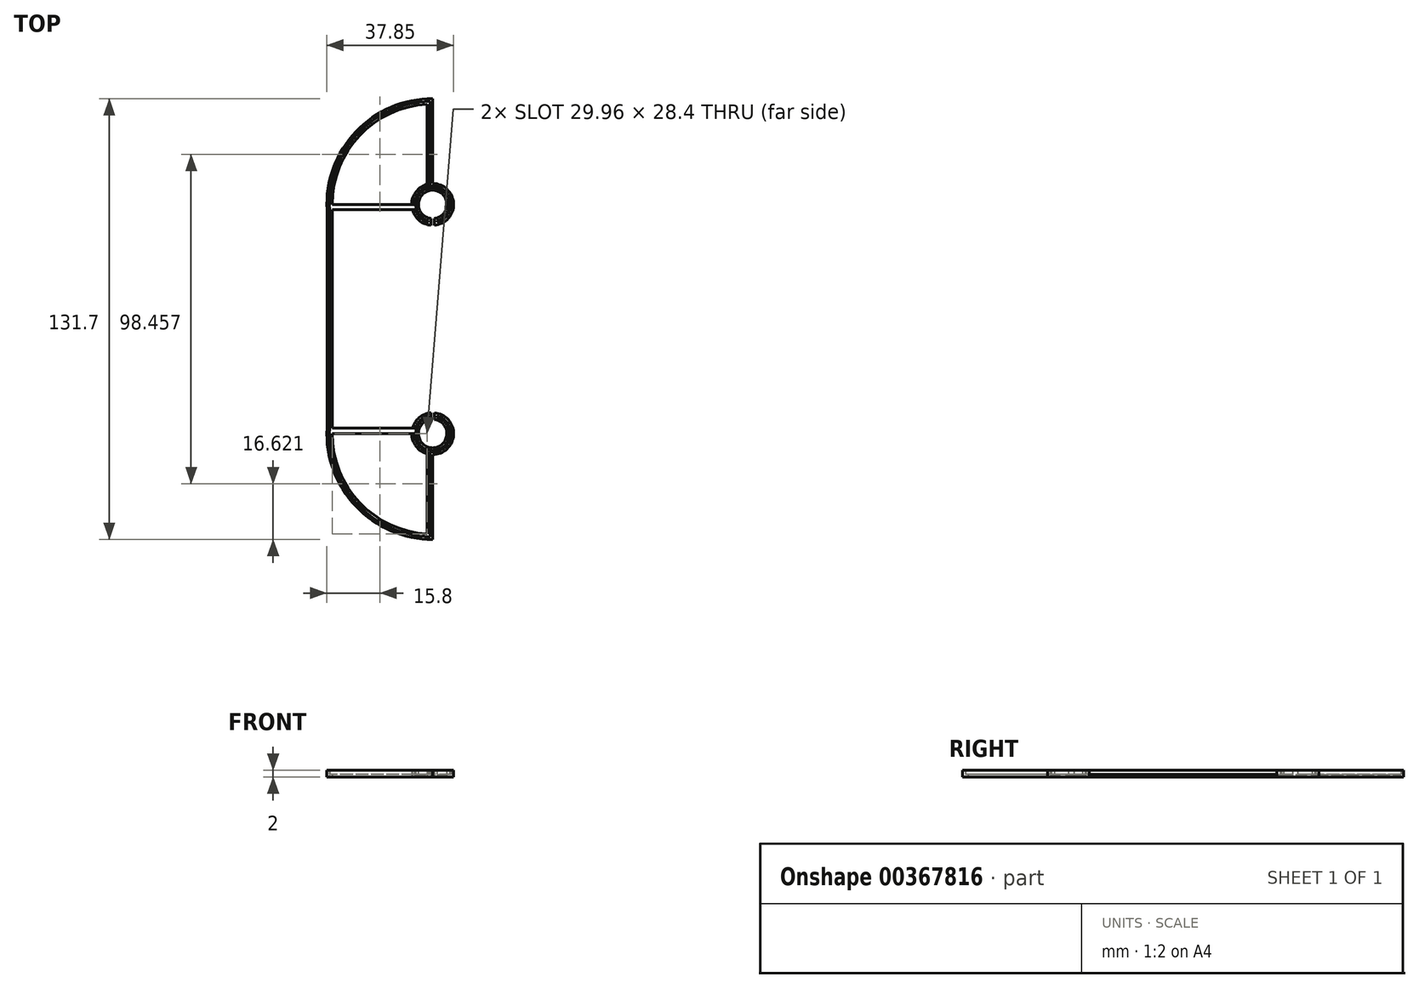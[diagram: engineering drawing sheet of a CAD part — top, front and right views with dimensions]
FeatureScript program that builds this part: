
annotation { "Feature Type Name" : "Feature", "Feature Type Description" : "" }
export const myFeature = defineFeature(function(context is Context, id is Id, definition is map)
    precondition{}
    {
        {
            var Q0;
            Q0=qCreatedBy(makeId("Top.planeOp"),FACE);
            var sketch = newSketch(context, id + "F0", { "sketchPlane" : qUnion([Q0])});
            skLineSegment(sketch, "E0.bottom", {"start": v(-34.25, -34.25) * mm, "end": v(34.25, -34.25) * mm, "construction": true});
            skLineSegment(sketch, "E0.top", {"start": v(-34.25, 34.25) * mm, "end": v(34.25, 34.25) * mm, "construction": true});
            skLineSegment(sketch, "E0.left", {"start": v(-34.25, -34.25) * mm, "end": v(-34.25, 34.25) * mm, "construction": true});
            skLineSegment(sketch, "E0.right", {"start": v(34.25, -34.25) * mm, "end": v(34.25, 34.25) * mm, "construction": true});
            skPoint(sketch, "E0.middle", {"position": v(0, 0) * mm});
            skLineSegment(sketch, "E1", {"start": v(0, 0) * mm, "end": v(0, 34.25) * mm, "construction": true});
            skLineSegment(sketch, "E2", {"start": v(0, 0) * mm, "end": v(-34.25, 0) * mm, "construction": true});
            skCircle(sketch, "E3", {"center": v(-34.25, 34.25) * mm, "radius": 4.25 * mm});
            skCircle(sketch, "E4", {"center": v(-34.25, 34.25) * mm, "radius": 6.25 * mm});
            skLineSegment(sketch, "E5", {"start": v(-34.75, 30.03) * mm, "end": v(-34.75, 28.02) * mm});
            skLineSegment(sketch, "E6.MirrorCS", {"start": v(-33.75, 30.03) * mm, "end": v(-33.75, 28.02) * mm});
            skCircle(sketch, "E7", {"center": v(-34.25, 34.25) * mm, "radius": 30 * mm, "construction": true});
            skCircle(sketch, "E8.MirrorC", {"center": v(34.25, 34.25) * mm, "radius": 6.25 * mm});
            skCircle(sketch, "E9.MirrorC", {"center": v(34.25, 34.25) * mm, "radius": 4.25 * mm});
            skCircle(sketch, "E10.MirrorC", {"center": v(34.25, 34.25) * mm, "radius": 30 * mm, "construction": true});
            skCircle(sketch, "E11.MirrorC", {"center": v(-34.25, -34.25) * mm, "radius": 4.25 * mm});
            skCircle(sketch, "E12.MirrorC", {"center": v(-34.25, -34.25) * mm, "radius": 6.25 * mm});
            skCircle(sketch, "E13.MirrorC", {"center": v(-34.25, -34.25) * mm, "radius": 30 * mm, "construction": true});
            skCircle(sketch, "E14.MirrorC", {"center": v(34.25, -34.25) * mm, "radius": 30 * mm, "construction": true});
            skCircle(sketch, "E15.MirrorC", {"center": v(34.25, -34.25) * mm, "radius": 6.25 * mm});
            skCircle(sketch, "E16.MirrorC", {"center": v(34.25, -34.25) * mm, "radius": 4.25 * mm});
            skLineSegment(sketch, "E17.MirrorCS", {"start": v(33.75, 30.03) * mm, "end": v(33.75, 28.02) * mm});
            skLineSegment(sketch, "E18.MirrorCS", {"start": v(34.75, 30.03) * mm, "end": v(34.75, 28.02) * mm});
            skLineSegment(sketch, "E19.MirrorCS", {"start": v(-34.75, -30.03) * mm, "end": v(-34.75, -28.02) * mm});
            skLineSegment(sketch, "E20.MirrorCS", {"start": v(-33.75, -30.03) * mm, "end": v(-33.75, -28.02) * mm});
            skLineSegment(sketch, "E21.MirrorCS", {"start": v(33.75, -30.03) * mm, "end": v(33.75, -28.02) * mm});
            skLineSegment(sketch, "E22.MirrorCS", {"start": v(34.75, -30.03) * mm, "end": v(34.75, -28.02) * mm});
            skLineSegment(sketch, "E23", {"start": v(-34.25, 40.5) * mm, "end": v(-34.25, 64.25) * mm});
            skLineSegment(sketch, "E24", {"start": v(-35.85, 40.3) * mm, "end": v(-35.85, 64.2) * mm});
            skLineSegment(sketch, "E25", {"start": v(-40.5, 34.25) * mm, "end": v(-64.25, 34.25) * mm});
            skLineSegment(sketch, "E26", {"start": v(-40.3, 32.65) * mm, "end": v(-64.2, 32.65) * mm});
            skArc(sketch, "E27", {"start": v(-34.25, 64.25) * mm, "mid": v(-56.02, 54.89) * mm, "end": v(-64.2, 32.65) * mm});
            skLineSegment(sketch, "E28", {"start": v(-34.25, 64.25) * mm, "end": v(-34.25, 65.85) * mm});
            skLineSegment(sketch, "E29", {"start": v(-64.2, 32.65) * mm, "end": v(-65.8, 32.65) * mm});
            skArc(sketch, "E30", {"start": v(-34.25, 65.85) * mm, "mid": v(-57.15, 56.02) * mm, "end": v(-65.8, 32.65) * mm});
            skLineSegment(sketch, "E31.MirrorCS", {"start": v(-40.3, -32.65) * mm, "end": v(-64.2, -32.65) * mm});
            skLineSegment(sketch, "E32.MirrorCS", {"start": v(-40.5, -34.25) * mm, "end": v(-64.25, -34.25) * mm});
            skLineSegment(sketch, "E33.MirrorCS", {"start": v(-64.2, -32.65) * mm, "end": v(-65.8, -32.65) * mm});
            skArc(sketch, "E34.MirrorCS", {"start": v(-34.25, -65.85) * mm, "mid": v(-57.15, -56.02) * mm, "end": v(-65.8, -32.65) * mm});
            skArc(sketch, "E35.MirrorCS", {"start": v(-34.25, -64.25) * mm, "mid": v(-56.02, -54.89) * mm, "end": v(-64.2, -32.65) * mm});
            skLineSegment(sketch, "E36.MirrorCS", {"start": v(-35.85, -40.3) * mm, "end": v(-35.85, -64.2) * mm});
            skLineSegment(sketch, "E37.MirrorCS", {"start": v(-34.25, -40.5) * mm, "end": v(-34.25, -64.25) * mm});
            skLineSegment(sketch, "E38.MirrorCS", {"start": v(-34.25, -64.25) * mm, "end": v(-34.25, -65.85) * mm});
            skLineSegment(sketch, "E39", {"start": v(-65.8, 32.65) * mm, "end": v(-65.8, -32.65) * mm});
            skLineSegment(sketch, "E40", {"start": v(-64.2, -32.65) * mm, "end": v(-64.2, 32.65) * mm});
            skSolve(sketch);
        }
        {
            var Q0;
            {var subQ0=sQuery(id+"F0.wireOp",EDGE,"E31.MirrorCS");Q0=makeQuery(id+"F0.imprint","IMPRINT",FACE,{"disambiguationData":[TD([[makeQuery(id+"F0.imprint","IMPRINT",EDGE,{"derivedFrom":subQ0}),1.0]])]});}
            var Q1;
            {var subQ5=sQuery(id+"F0.wireOp",EDGE,"E19.MirrorCS");Q1=makeQuery(id+"F0.imprint","IMPRINT",FACE,{"disambiguationData":[TD([[makeQuery(id+"F0.imprint","IMPRINT",EDGE,{"derivedFrom":subQ5}),1.0]])]});}
            var Q2;
            {var subQ0=sQuery(id+"F0.wireOp",EDGE,"E36.MirrorCS");Q2=makeQuery(id+"F0.imprint","IMPRINT",FACE,{"disambiguationData":[TD([[makeQuery(id+"F0.imprint","IMPRINT",EDGE,{"derivedFrom":subQ0}),1.0]])]});}
            var Q3;
            {var subQ4=sQuery(id+"F0.wireOp",EDGE,"E33.MirrorCS");Q3=makeQuery(id+"F0.imprint","IMPRINT",FACE,{"disambiguationData":[TD([[makeQuery(id+"F0.imprint","IMPRINT",EDGE,{"derivedFrom":subQ4}),1.0]])]});}
            var Q4;
            Q4=makeQuery(id+"F0.imprint","IMPRINT",FACE,{"disambiguationData":[TD([[makeQuery(id+"F0.imprint","IMPRINT",EDGE,{"derivedFrom":sQuery(id+"F0.wireOp",EDGE,"E29")}),1.0]])]});
            var Q5;
            {var subQ0=sQuery(id+"F0.wireOp",EDGE,"E28");Q5=makeQuery(id+"F0.imprint","IMPRINT",FACE,{"disambiguationData":[TD([[makeQuery(id+"F0.imprint","IMPRINT",EDGE,{"derivedFrom":subQ0}),1.0]])]});}
            var Q6;
            {var subQ0=sQuery(id+"F0.wireOp",EDGE,"E25");Q6=makeQuery(id+"F0.imprint","IMPRINT",FACE,{"disambiguationData":[TD([[makeQuery(id+"F0.imprint","IMPRINT",EDGE,{"derivedFrom":subQ0}),1.0]])]});}
            var Q7;
            {var subQ5=sQuery(id+"F0.wireOp",EDGE,"E5");Q7=makeQuery(id+"F0.imprint","IMPRINT",FACE,{"disambiguationData":[TD([[makeQuery(id+"F0.imprint","IMPRINT",EDGE,{"derivedFrom":subQ5}),-1.0]])]});}
            var Q8;
            {var subQ0=sQuery(id+"F0.wireOp",EDGE,"E23");Q8=makeQuery(id+"F0.imprint","IMPRINT",FACE,{"disambiguationData":[TD([[makeQuery(id+"F0.imprint","IMPRINT",EDGE,{"derivedFrom":subQ0}),1.0]])]});}
            extrude(context, id + "F1", {"entities" : qUnion([Q0, Q1, Q2, Q3, Q4, Q5, Q6, Q7, Q8]), "depth" : 2 * mm});
        }
        {
            var Q0;
            Q0=makeQuery(id+"F1.opExtrude","SWEPT_FACE",FACE,{"disambiguationData":[OSD([sQuery(id+"F0.wireOp",EDGE,"E40")])]});
            var Q1;
            Q1=makeQuery(id+"F1.opExtrude","SWEPT_FACE",FACE,{"disambiguationData":[OSD([sQuery(id+"F0.wireOp",EDGE,"E35.MirrorCS")])]});
            var Q2;
            Q2=makeQuery(id+"F1.opExtrude","CAP_FACE",FACE,{"disambiguationData":[OSD([sQuery(id+"F0.wireOp",EDGE,"E3"),sQuery(id+"F0.wireOp",EDGE,"E4"),sQuery(id+"F0.wireOp",EDGE,"E5"),sQuery(id+"F0.wireOp",EDGE,"E6.MirrorCS"),sQuery(id+"F0.wireOp",EDGE,"E11.MirrorC"),sQuery(id+"F0.wireOp",EDGE,"E12.MirrorC"),sQuery(id+"F0.wireOp",EDGE,"E19.MirrorCS"),sQuery(id+"F0.wireOp",EDGE,"E20.MirrorCS"),sQuery(id+"F0.wireOp",EDGE,"E23"),sQuery(id+"F0.wireOp",EDGE,"E24"),sQuery(id+"F0.wireOp",EDGE,"E25"),sQuery(id+"F0.wireOp",EDGE,"E26"),sQuery(id+"F0.wireOp",EDGE,"E27"),sQuery(id+"F0.wireOp",EDGE,"E28"),sQuery(id+"F0.wireOp",EDGE,"E30"),sQuery(id+"F0.wireOp",EDGE,"E31.MirrorCS"),sQuery(id+"F0.wireOp",EDGE,"E32.MirrorCS"),sQuery(id+"F0.wireOp",EDGE,"E34.MirrorCS"),sQuery(id+"F0.wireOp",EDGE,"E35.MirrorCS"),sQuery(id+"F0.wireOp",EDGE,"E36.MirrorCS"),sQuery(id+"F0.wireOp",EDGE,"E37.MirrorCS"),sQuery(id+"F0.wireOp",EDGE,"E38.MirrorCS"),sQuery(id+"F0.wireOp",EDGE,"E39"),sQuery(id+"F0.wireOp",EDGE,"E40")])],"isStart":false});
            var Q3;
            Q3=makeQuery(id+"F1.opExtrude","SWEPT_FACE",FACE,{"disambiguationData":[OSD([sQuery(id+"F0.wireOp",EDGE,"E27")])]});
            var Q4;
            Q4=makeQuery(id+"F1.opExtrude","SWEPT_FACE",FACE,{"disambiguationData":[OSD([sQuery(id+"F0.wireOp",EDGE,"E24")])]});
            var Q5;
            Q5=makeQuery(id+"F1.opExtrude","SWEPT_FACE",FACE,{"disambiguationData":[OSD([sQuery(id+"F0.wireOp",EDGE,"E25")])]});
            var Q6;
            Q6=makeQuery(id+"F1.opExtrude","SWEPT_FACE",FACE,{"disambiguationData":[OSD([sQuery(id+"F0.wireOp",EDGE,"E26")])]});
            var Q7;
            Q7=makeQuery(id+"F1.opExtrude","SWEPT_FACE",FACE,{"disambiguationData":[OSD([sQuery(id+"F0.wireOp",EDGE,"E32.MirrorCS")])]});
            var Q8;
            Q8=makeQuery(id+"F1.opExtrude","SWEPT_FACE",FACE,{"disambiguationData":[OSD([sQuery(id+"F0.wireOp",EDGE,"E31.MirrorCS")])]});
            var Q9;
            Q9=makeQuery(id+"F1.opExtrude","SWEPT_FACE",FACE,{"disambiguationData":[OSD([sQuery(id+"F0.wireOp",EDGE,"E36.MirrorCS")])]});
            shell(context, id + "F2", {"entities" : qUnion([Q0, Q1, Q2, Q3, Q4, Q5, Q6, Q7, Q8, Q9]), "thickness" : .8 * mm});
        }
    });
